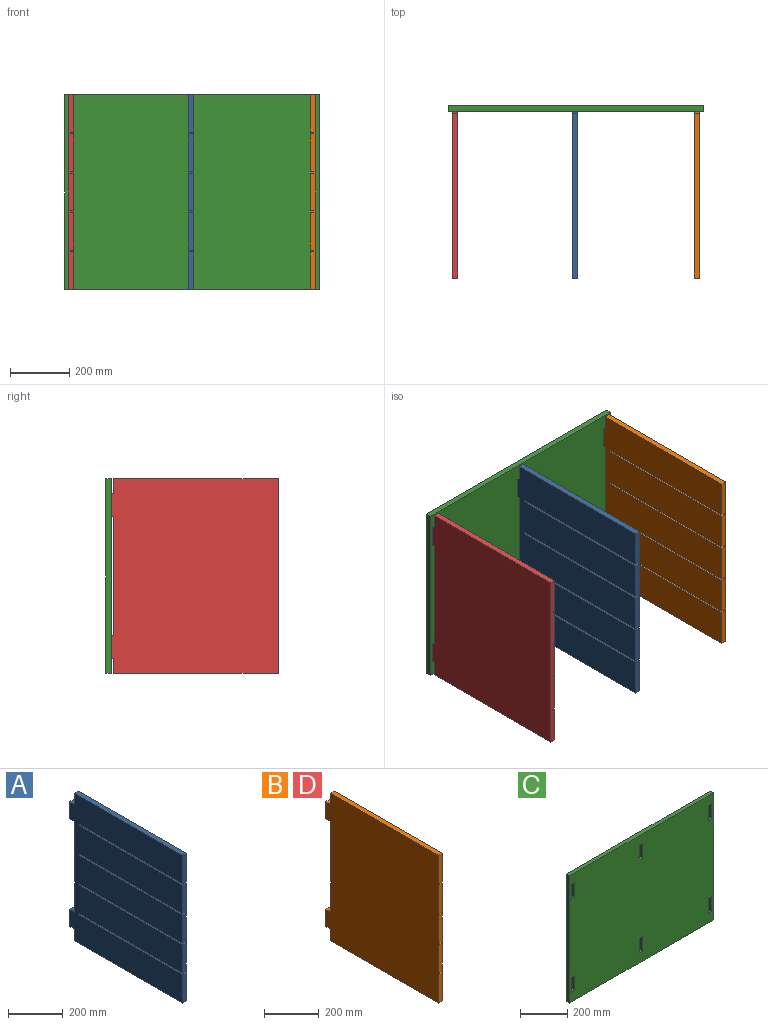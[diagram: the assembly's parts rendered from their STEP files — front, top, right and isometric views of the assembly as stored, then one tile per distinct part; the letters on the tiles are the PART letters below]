
ASSEMBLY  parts=4 mates=3
PART A: 30 faces, bbox 19.1x584.2x660.4 mm
  f0: plane 406.4x19.05mm, normal (0,1,0), area 7741.9mm2, adj f1,f27,f28,f29
  f1: plane 25.4x19.05mm, normal (0,0,-1), area 483.9mm2, adj f0,f2,f28,f29
  f2: plane 76.2x19.05mm, normal (0,1,0), area 1451.6mm2, adj f1,f3,f28,f29
  f3: plane 25.4x19.05mm, normal (0,0,1), area 483.9mm2, adj f2,f4,f28,f29
  f4: plane 50.8x19.05mm, normal (0,1,0), area 967.7mm2, adj f3,f5,f28,f29
  f5: plane 558.8x19.05mm, normal (0,0,1), area 10645.1mm2, adj f4,f6,f28,f29
  f6: plane 127x19.05mm, normal (0,-1,0), area 2419.3mm2, adj f5,f7,f28,f29
  f7: plane 533.4x19.05mm, normal (0,0,-1), area 10161.3mm2, adj f6,f8,f28,f29
  f8: plane 19.05x6.35mm, normal (0,-1,0), area 121mm2, adj f7,f9,f28,f29
  f9: plane 533.4x19.05mm, normal (0,0,1), area 10161.3mm2, adj f8,f10,f28,f29
  f10: plane 127x19.05mm, normal (0,-1,0), area 2419.3mm2, adj f9,f11,f28,f29
  f11: plane 533.4x19.05mm, normal (0,0,-1), area 10161.3mm2, adj f10,f12,f28,f29
  f12: plane 19.05x6.35mm, normal (0,-1,0), area 121mm2, adj f11,f13,f28,f29
  f13: plane 533.4x19.05mm, normal (0,0,1), area 10161.3mm2, adj f12,f14,f28,f29
  f14: plane 127x19.05mm, normal (0,-1,0), area 2419.3mm2, adj f13,f15,f28,f29
  f15: plane 533.4x19.05mm, normal (0,0,-1), area 10161.3mm2, adj f14,f16,f28,f29
  f16: plane 19.05x6.35mm, normal (0,-1,0), area 121mm2, adj f15,f17,f28,f29
  f17: plane 533.4x19.05mm, normal (0,0,1), area 10161.3mm2, adj f16,f18,f28,f29
  f18: plane 127x19.05mm, normal (0,-1,0), area 2419.3mm2, adj f17,f19,f28,f29
  f19: plane 533.4x19.05mm, normal (0,0,-1), area 10161.3mm2, adj f18,f20,f28,f29
  f20: plane 19.05x6.35mm, normal (0,-1,0), area 121mm2, adj f19,f21,f28,f29
  f21: plane 533.4x19.05mm, normal (0,0,1), area 10161.3mm2, adj f20,f22,f28,f29
  f22: plane 127x19.05mm, normal (0,-1,0), area 2419.3mm2, adj f21,f23,f28,f29
  f23: plane 558.8x19.05mm, normal (0,0,-1), area 10645.1mm2, adj f22,f24,f28,f29
  f24: plane 50.8x19.05mm, normal (0,1,0), area 967.7mm2, adj f23,f25,f28,f29
  f25: plane 25.4x19.05mm, normal (0,0,-1), area 483.9mm2, adj f24,f26,f28,f29
  f26: plane 76.2x19.05mm, normal (0,1,0), area 1451.6mm2, adj f25,f27,f28,f29
  f27: plane 25.4x19.05mm, normal (0,0,1), area 483.9mm2, adj f0,f26,f28,f29
  f28: plane 660.4x584.2mm, normal (1,0,0), area 359354.1mm2, adj f0,f1,f2,f3,f4,f5,f6,f7
  f29: plane 660.4x584.2mm, normal (-1,0,0), area 359354.1mm2, adj f0,f1,f2,f3,f4,f5,f6,f7
PART B: 30 faces, bbox 19.1x584.2x660.4 mm
  f0: plane 406.4x19.05mm, normal (0,1,0), area 7741.9mm2, adj f1,f23,f24,f25
  f1: plane 25.4x19.05mm, normal (0,0,-1), area 483.9mm2, adj f0,f2,f24,f25
  f2: plane 76.2x19.05mm, normal (0,1,0), area 1451.6mm2, adj f1,f3,f24,f25
  f3: plane 25.4x19.05mm, normal (0,0,1), area 483.9mm2, adj f2,f4,f24,f25
  f4: plane 50.8x19.05mm, normal (0,1,0), area 967.7mm2, adj f3,f5,f24,f25
  f5: plane 558.8x19.05mm, normal (0,0,1), area 10645.1mm2, adj f4,f18,f24,f25
  f6: plane 533.4x12.7mm, normal (0,0,-1), area 6774.2mm2, adj f7,f18,f24,f26
  f7: plane 12.7x6.35mm, normal (0,-1,0), area 80.6mm2, adj f6,f8,f24,f26
  f8: plane 533.4x12.7mm, normal (0,0,1), area 6774.2mm2, adj f7,f18,f24,f26
  f9: plane 533.4x12.7mm, normal (0,0,-1), area 6774.2mm2, adj f10,f18,f24,f28
  f10: plane 12.7x6.35mm, normal (0,-1,0), area 80.6mm2, adj f9,f11,f24,f28
  f11: plane 533.4x12.7mm, normal (0,0,1), area 6774.2mm2, adj f10,f18,f24,f28
  f12: plane 533.4x12.7mm, normal (0,0,-1), area 6774.2mm2, adj f13,f18,f24,f27
  f13: plane 12.7x6.35mm, normal (0,-1,0), area 80.6mm2, adj f12,f14,f24,f27
  f14: plane 533.4x12.7mm, normal (0,0,1), area 6774.2mm2, adj f13,f18,f24,f27
  f15: plane 533.4x12.7mm, normal (0,0,-1), area 6774.2mm2, adj f16,f18,f24,f29
  f16: plane 12.7x6.35mm, normal (0,-1,0), area 80.6mm2, adj f15,f17,f24,f29
  f17: plane 533.4x12.7mm, normal (0,0,1), area 6774.2mm2, adj f16,f18,f24,f29
  f18: plane 660.4x19.05mm, normal (0,-1,0), area 12258mm2, adj f5,f6,f8,f9,f11,f12,f14,f15
  f19: plane 558.8x19.05mm, normal (0,0,-1), area 10645.1mm2, adj f18,f20,f24,f25
  f20: plane 50.8x19.05mm, normal (0,1,0), area 967.7mm2, adj f19,f21,f24,f25
  f21: plane 25.4x19.05mm, normal (0,0,-1), area 483.9mm2, adj f20,f22,f24,f25
  f22: plane 76.2x19.05mm, normal (0,1,0), area 1451.6mm2, adj f21,f23,f24,f25
  f23: plane 25.4x19.05mm, normal (0,0,1), area 483.9mm2, adj f0,f22,f24,f25
  f24: plane 660.4x584.2mm, normal (1,0,0), area 359354.1mm2, adj f0,f1,f2,f3,f4,f5,f6,f7
  f25: plane 660.4x584.2mm, normal (-1,0,0), area 372902.5mm2, adj f0,f1,f2,f3,f4,f5,f18,f19
  f26: plane 533.4x6.35mm, normal (1,0,0), area 3387.1mm2, adj f6,f7,f8,f18
  f27: plane 533.4x6.35mm, normal (1,0,0), area 3387.1mm2, adj f12,f13,f14,f18
  f28: plane 533.4x6.35mm, normal (1,0,0), area 3387.1mm2, adj f9,f10,f11,f18
  f29: plane 533.4x6.35mm, normal (1,0,0), area 3387.1mm2, adj f15,f16,f17,f18
PART C: 30 faces, bbox 863.6x19.1x660.4 mm
  f0: plane 863.6x19.05mm, normal (0,0,1), area 16451.6mm2, adj f1,f27,f28,f29
  f1: plane 660.4x19.05mm, normal (-1,0,0), area 12580.6mm2, adj f0,f2,f28,f29
  f2: plane 863.6x19.05mm, normal (0,0,-1), area 16451.6mm2, adj f1,f27,f28,f29
  f3: plane 76.2x19.05mm, normal (1,0,0), area 1451.6mm2, adj f4,f21,f28,f29
  f4: plane 19.05x19.05mm, normal (0,0,-1), area 362.9mm2, adj f3,f5,f28,f29
  f5: plane 76.2x19.05mm, normal (-1,0,0), area 1451.6mm2, adj f4,f21,f28,f29
  f6: plane 76.2x19.05mm, normal (1,0,0), area 1451.6mm2, adj f7,f22,f28,f29
  f7: plane 19.05x19.05mm, normal (0,0,-1), area 362.9mm2, adj f6,f8,f28,f29
  f8: plane 76.2x19.05mm, normal (-1,0,0), area 1451.6mm2, adj f7,f22,f28,f29
  f9: plane 76.2x19.05mm, normal (1,0,0), area 1451.6mm2, adj f10,f23,f28,f29
  f10: plane 19.05x19.05mm, normal (0,0,-1), area 362.9mm2, adj f9,f11,f28,f29
  f11: plane 76.2x19.05mm, normal (-1,0,0), area 1451.6mm2, adj f10,f23,f28,f29
  f12: plane 76.2x19.05mm, normal (1,0,0), area 1451.6mm2, adj f13,f24,f28,f29
  f13: plane 19.05x19.05mm, normal (0,0,-1), area 362.9mm2, adj f12,f14,f28,f29
  f14: plane 76.2x19.05mm, normal (-1,0,0), area 1451.6mm2, adj f13,f24,f28,f29
  f15: plane 76.2x19.05mm, normal (1,0,0), area 1451.6mm2, adj f16,f25,f28,f29
  f16: plane 19.05x19.05mm, normal (0,0,-1), area 362.9mm2, adj f15,f17,f28,f29
  f17: plane 76.2x19.05mm, normal (-1,0,0), area 1451.6mm2, adj f16,f25,f28,f29
  f18: plane 76.2x19.05mm, normal (1,0,0), area 1451.6mm2, adj f19,f26,f28,f29
  f19: plane 19.05x19.05mm, normal (0,0,-1), area 362.9mm2, adj f18,f20,f28,f29
  f20: plane 76.2x19.05mm, normal (-1,0,0), area 1451.6mm2, adj f19,f26,f28,f29
  f21: plane 19.05x19.05mm, normal (0,0,1), area 362.9mm2, adj f3,f5,f28,f29
  f22: plane 19.05x19.05mm, normal (0,0,1), area 362.9mm2, adj f6,f8,f28,f29
  f23: plane 19.05x19.05mm, normal (0,0,1), area 362.9mm2, adj f9,f11,f28,f29
  f24: plane 19.05x19.05mm, normal (0,0,1), area 362.9mm2, adj f12,f14,f28,f29
  f25: plane 19.05x19.05mm, normal (0,0,1), area 362.9mm2, adj f15,f17,f28,f29
  f26: plane 19.05x19.05mm, normal (0,0,1), area 362.9mm2, adj f18,f20,f28,f29
  f27: plane 660.4x19.05mm, normal (1,0,0), area 12580.6mm2, adj f0,f2,f28,f29
  f28: plane 863.6x660.4mm, normal (0,-1,0), area 561611.8mm2, adj f0,f1,f2,f3,f4,f5,f6,f7
  f29: plane 863.6x660.4mm, normal (0,1,0), area 561611.8mm2, adj f0,f1,f2,f3,f4,f5,f6,f7
PART D: same geometry as B
PLACE A rot(axis=(0.87,0.49,0.01),0deg) t=(215.36,-579.25,-18.09)mm
PLACE B rot(axis=(0,-1,0),180deg) t=(647.16,-593.78,80.16)mm
PLACE C rot(axis=(0.87,0.49,0.01),0deg) t=(-82.37,-301.01,-72.36)mm
PLACE D rot(axis=(0.87,0.49,0.01),0deg) t=(-191.04,-593.78,-77.85)mm
MATE fastened A.f25 <-> C.f26  axis (0,0,-1) through (234.41,-301.01,-278.24)mm
MATE fastened B.f21 <-> C.f10  axis (0,0,1) through (647.16,-301.01,280.56)mm
MATE fastened D.f2 <-> C.f29  axis (0,1,0) through (-191.04,-301.01,280.56)mm
